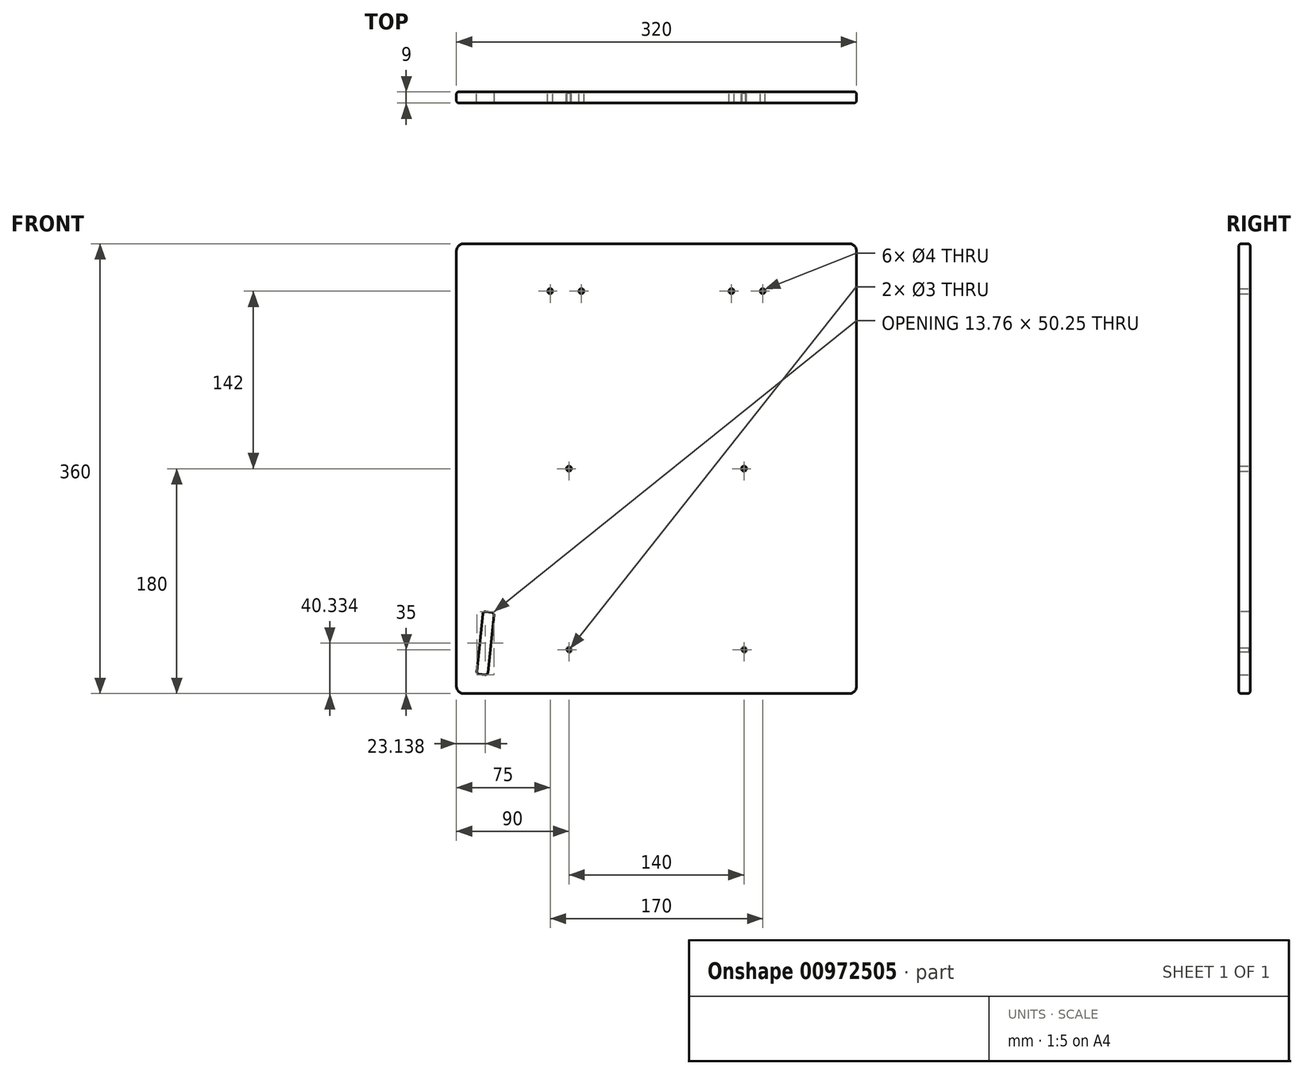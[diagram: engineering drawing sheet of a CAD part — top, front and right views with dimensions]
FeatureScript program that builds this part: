
annotation { "Feature Type Name" : "Feature", "Feature Type Description" : "" }
export const myFeature = defineFeature(function(context is Context, id is Id, definition is map)
    precondition{}
    {
        {
            var Q0;
            Q0=qCreatedBy(makeId("Front.planeOp"),FACE);
            var sketch = newSketch(context, id + "F0", { "sketchPlane" : qUnion([Q0])});
            skLineSegment(sketch, "E0.bottom", {"start": v(-160, 360) * mm, "end": v(160, 360) * mm});
            skLineSegment(sketch, "E0.top", {"start": v(-160, 0) * mm, "end": v(160, 0) * mm});
            skLineSegment(sketch, "E0.left", {"start": v(-160, 360) * mm, "end": v(-160, 0) * mm});
            skLineSegment(sketch, "E0.right", {"start": v(160, 360) * mm, "end": v(160, 0) * mm});
            skSolve(sketch);
        }
        {
            var Q0;
            Q0=makeQuery(id+"F0.imprint","IMPRINT",FACE,{"disambiguationData":[TD([[makeQuery(id+"F0.imprint","IMPRINT",EDGE,{"derivedFrom":sQuery(id+"F0.wireOp",EDGE,"E0.bottom")}),-1.0]])]});
            extrude(context, id + "F1", {"entities" : qUnion([Q0]), "oppositeDirection" : true, "depth" : 9 * mm, "offsetDistance" : 25 * mm});
        }
        {
            var Q0;
            Q0=qCreatedBy(makeId("Front.planeOp"),FACE);
            var sketch = newSketch(context, id + "F2", { "sketchPlane" : qUnion([Q0])});
            skLineSegment(sketch, "E1", {"start": v(-138.72, 65.67) * mm, "end": v(-143.95, 15.94) * mm});
            skLineSegment(sketch, "E2", {"start": v(-135, 15) * mm, "end": v(-129.77, 64.73) * mm});
            skLineSegment(sketch, "E3", {"start": v(-138.72, 65.67) * mm, "end": v(-129.77, 64.73) * mm});
            skLineSegment(sketch, "E4", {"start": v(-143.95, 15.94) * mm, "end": v(-135, 15) * mm});
            skSolve(sketch);
        }
        {
            var Q0;
            Q0=makeQuery(id+"F2.imprint","IMPRINT",FACE,{"disambiguationData":[TD([[makeQuery(id+"F2.imprint","IMPRINT",EDGE,{"derivedFrom":sQuery(id+"F2.wireOp",EDGE,"E1")}),1.0]])]});
            var Q1;
            Q1=makeQuery(id+"F2.imprint","IMPRINT",FACE,{"disambiguationData":[TD([[makeQuery(id+"F2.imprint","IMPRINT",EDGE,{"derivedFrom":sQuery(id+"F2.wireOp",EDGE,"cv69mtFc-LBA8-5CoM-4E6C-DW0wjyTnq0Fr")}),1.0]])]});
            var Q2;
            Q2=makeQuery(id+"F2.imprint","IMPRINT",FACE,{"disambiguationData":[TD([[makeQuery(id+"F2.imprint","IMPRINT",EDGE,{"derivedFrom":sQuery(id+"F2.wireOp",EDGE,"YBglI7SL-vM7m-gSXs-ycqa-cWJAcuNKxBdc.bottom")}),-1.0]])]});
            extrude(context, id + "F3", {"entities" : qUnion([Q0, Q1, Q2]), "operationType" : NewBodyOperationType.REMOVE, "endBound" : BoundingType.THROUGH_ALL, "oppositeDirection" : true, "depth" : 25 * mm, "offsetDistance" : 25 * mm});
        }
        {
            var Q0;
            Q0=makeQuery(id+"F3.boolean.opBoolean","COPY",EDGE,{"derivedFrom":makeQuery(id+"F3.opExtrude","SWEPT_EDGE",EDGE,{"disambiguationData":[OSD([sQuery(id+"F2.wireOp",EDGE,"E2"),sQuery(id+"F2.wireOp",EDGE,"E4")])]})});
            var Q1;
            Q1=makeQuery(id+"F3.boolean.opBoolean","COPY",EDGE,{"derivedFrom":makeQuery(id+"F3.opExtrude","SWEPT_EDGE",EDGE,{"disambiguationData":[OSD([sQuery(id+"F2.wireOp",EDGE,"E1"),sQuery(id+"F2.wireOp",EDGE,"E4")])]})});
            var Q2;
            Q2=makeQuery(id+"F3.boolean.opBoolean","COPY",EDGE,{"derivedFrom":makeQuery(id+"F3.opExtrude","SWEPT_EDGE",EDGE,{"disambiguationData":[OSD([sQuery(id+"F2.wireOp",EDGE,"E2"),sQuery(id+"F2.wireOp",EDGE,"E3")])]})});
            var Q3;
            Q3=makeQuery(id+"F3.boolean.opBoolean","COPY",EDGE,{"derivedFrom":makeQuery(id+"F3.opExtrude","SWEPT_EDGE",EDGE,{"disambiguationData":[OSD([sQuery(id+"F2.wireOp",EDGE,"E1"),sQuery(id+"F2.wireOp",EDGE,"E3")])]})});
            var Q4;
            Q4=makeQuery(id+"F3.boolean.opBoolean","COPY",EDGE,{"derivedFrom":makeQuery(id+"F3.opExtrude","SWEPT_EDGE",EDGE,{"disambiguationData":[OSD([sQuery(id+"F2.wireOp",EDGE,"cv69mtFc-LBA8-5CoM-4E6C-DW0wjyTnq0Fr"),sQuery(id+"F2.wireOp",EDGE,"zAuP8GzA-tnE1-vwlP-NUoL-qnI0OchEDumV")])]})});
            var Q5;
            Q5=makeQuery(id+"F3.boolean.opBoolean","COPY",EDGE,{"derivedFrom":makeQuery(id+"F3.opExtrude","SWEPT_EDGE",EDGE,{"disambiguationData":[OSD([sQuery(id+"F2.wireOp",EDGE,"cv69mtFc-LBA8-5CoM-4E6C-DW0wjyTnq0Fr"),sQuery(id+"F2.wireOp",EDGE,"tRgE08ra-H2Sr-GnxG-apVD-usmjHhvz710O")])]})});
            var Q6;
            Q6=makeQuery(id+"F3.boolean.opBoolean","COPY",EDGE,{"derivedFrom":makeQuery(id+"F3.opExtrude","SWEPT_EDGE",EDGE,{"disambiguationData":[OSD([sQuery(id+"F2.wireOp",EDGE,"zAuP8GzA-tnE1-vwlP-NUoL-qnI0OchEDumV"),sQuery(id+"F2.wireOp",EDGE,"MxeWzJpH-qL4w-clRe-FggT-xUZ2qBjI2IpG")])]})});
            var Q7;
            Q7=makeQuery(id+"F3.boolean.opBoolean","COPY",EDGE,{"derivedFrom":makeQuery(id+"F3.opExtrude","SWEPT_EDGE",EDGE,{"disambiguationData":[OSD([sQuery(id+"F2.wireOp",EDGE,"tRgE08ra-H2Sr-GnxG-apVD-usmjHhvz710O"),sQuery(id+"F2.wireOp",EDGE,"MxeWzJpH-qL4w-clRe-FggT-xUZ2qBjI2IpG")])]})});
            var Q8;
            Q8=makeQuery(id+"F3.boolean.opBoolean","COPY",EDGE,{"derivedFrom":makeQuery(id+"F3.opExtrude","SWEPT_EDGE",EDGE,{"disambiguationData":[OSD([sQuery(id+"F2.wireOp",EDGE,"YBglI7SL-vM7m-gSXs-ycqa-cWJAcuNKxBdc.top"),sQuery(id+"F2.wireOp",EDGE,"YBglI7SL-vM7m-gSXs-ycqa-cWJAcuNKxBdc.right")])]})});
            var Q9;
            Q9=makeQuery(id+"F3.boolean.opBoolean","COPY",EDGE,{"derivedFrom":makeQuery(id+"F3.opExtrude","SWEPT_EDGE",EDGE,{"disambiguationData":[OSD([sQuery(id+"F2.wireOp",EDGE,"YBglI7SL-vM7m-gSXs-ycqa-cWJAcuNKxBdc.top"),sQuery(id+"F2.wireOp",EDGE,"YBglI7SL-vM7m-gSXs-ycqa-cWJAcuNKxBdc.left")])]})});
            var Q10;
            Q10=makeQuery(id+"F3.boolean.opBoolean","COPY",EDGE,{"derivedFrom":makeQuery(id+"F3.opExtrude","SWEPT_EDGE",EDGE,{"disambiguationData":[OSD([sQuery(id+"F2.wireOp",EDGE,"YBglI7SL-vM7m-gSXs-ycqa-cWJAcuNKxBdc.bottom"),sQuery(id+"F2.wireOp",EDGE,"YBglI7SL-vM7m-gSXs-ycqa-cWJAcuNKxBdc.right")])]})});
            var Q11;
            Q11=makeQuery(id+"F3.boolean.opBoolean","COPY",EDGE,{"derivedFrom":makeQuery(id+"F3.opExtrude","SWEPT_EDGE",EDGE,{"disambiguationData":[OSD([sQuery(id+"F2.wireOp",EDGE,"YBglI7SL-vM7m-gSXs-ycqa-cWJAcuNKxBdc.bottom"),sQuery(id+"F2.wireOp",EDGE,"YBglI7SL-vM7m-gSXs-ycqa-cWJAcuNKxBdc.left")])]})});
            fillet(context, id + "F4", {"entities" : qUnion([Q0, Q1, Q2, Q3, Q4, Q5, Q6, Q7, Q8, Q9, Q10, Q11]), "radius" : 2 * mm, "tangentPropagation" : true, "allowEdgeOverflow" : false});
        }
        {
            var Q0;
            Q0=makeQuery(id+"F1.opExtrude","SWEPT_EDGE",EDGE,{"disambiguationData":[OSD([sQuery(id+"F0.wireOp",EDGE,"E0.top"),sQuery(id+"F0.wireOp",EDGE,"E0.right")])]});
            var Q1;
            Q1=makeQuery(id+"F1.opExtrude","SWEPT_EDGE",EDGE,{"disambiguationData":[OSD([sQuery(id+"F0.wireOp",EDGE,"E0.bottom"),sQuery(id+"F0.wireOp",EDGE,"E0.right")])]});
            var Q2;
            Q2=makeQuery(id+"F1.opExtrude","SWEPT_EDGE",EDGE,{"disambiguationData":[OSD([sQuery(id+"F0.wireOp",EDGE,"E0.bottom"),sQuery(id+"F0.wireOp",EDGE,"E0.left")])]});
            var Q3;
            Q3=makeQuery(id+"F1.opExtrude","SWEPT_EDGE",EDGE,{"disambiguationData":[OSD([sQuery(id+"F0.wireOp",EDGE,"E0.top"),sQuery(id+"F0.wireOp",EDGE,"E0.left")])]});
            fillet(context, id + "F5", {"entities" : qUnion([Q0, Q1, Q2, Q3]), "radius" : 6 * mm, "tangentPropagation" : true, "allowEdgeOverflow" : false});
        }
        {
            var Q0;
            Q0=makeQuery(id+"F1.opExtrude","CAP_FACE",FACE,{"disambiguationData":[OSD([sQuery(id+"F0.wireOp",EDGE,"E0.bottom"),sQuery(id+"F0.wireOp",EDGE,"E0.top"),sQuery(id+"F0.wireOp",EDGE,"E0.left"),sQuery(id+"F0.wireOp",EDGE,"E0.right")])],"isStart":false});
            var sketch = newSketch(context, id + "F6", { "sketchPlane" : qUnion([Q0])});
            skPoint(sketch, "E5", {"position": v(-70, 35) * mm});
            skPoint(sketch, "E6", {"position": v(70, 35) * mm});
            skLineSegment(sketch, "E7", {"start": v(-70, 35) * mm, "end": v(70, 35) * mm, "construction": true});
            skLineSegment(sketch, "E8", {"start": v(0, 35) * mm, "end": v(0, 0) * mm, "construction": true});
            skSolve(sketch);
        }
        {
            var Q0;
            Q0=sQuery(id+"F6.wireOp",VERTEX,"E5");
            var Q1;
            Q1=sQuery(id+"F6.wireOp",VERTEX,"E6");
            var Q2;
            Q2=makeQuery(id+"F1.opExtrude","SWEPT_BODY",BODY,{"disambiguationData":[OSD([sQuery(id+"F0.wireOp",EDGE,"E0.bottom"),sQuery(id+"F0.wireOp",EDGE,"E0.top"),sQuery(id+"F0.wireOp",EDGE,"E0.left"),sQuery(id+"F0.wireOp",EDGE,"E0.right")])]});
            hole(context, id + "F7", {"style" : HoleStyle.C_SINK, "endStyle" : HoleEndStyle.THROUGH, "holeDiameter" : 3 * mm, "cSinkDiameter" : 5 * mm, "cSinkAngle" : 90 * degree, "majorDiameter" : 5 * mm, "isTappedThrough" : true, "tappedDepth" : 12 * mm, "tapClearance" : 3, "locations" : qUnion([Q0, Q1]), "scope" : qUnion([Q2])});
        }
        {
            var Q0;
            Q0=makeQuery(id+"F1.opExtrude","CAP_FACE",FACE,{"disambiguationData":[OSD([sQuery(id+"F0.wireOp",EDGE,"E0.bottom"),sQuery(id+"F0.wireOp",EDGE,"E0.top"),sQuery(id+"F0.wireOp",EDGE,"E0.left"),sQuery(id+"F0.wireOp",EDGE,"E0.right")])],"isStart":false});
            var sketch = newSketch(context, id + "F8", { "sketchPlane" : qUnion([Q0])});
            skLineSegment(sketch, "E9", {"start": v(-70, 180) * mm, "end": v(70, 180) * mm, "construction": true});
            skLineSegment(sketch, "E10", {"start": v(0, 180) * mm, "end": v(0, 0) * mm, "construction": true});
            skPoint(sketch, "E11", {"position": v(-70, 180) * mm});
            skPoint(sketch, "E12", {"position": v(70, 180) * mm});
            skLineSegment(sketch, "E13", {"start": v(85, 322) * mm, "end": v(60, 322) * mm, "construction": true});
            skPoint(sketch, "E14", {"position": v(85, 322) * mm});
            skPoint(sketch, "E15", {"position": v(60, 322) * mm});
            skPoint(sketch, "E16", {"position": v(-60, 322) * mm});
            skPoint(sketch, "E17", {"position": v(-85, 322) * mm});
            skLineSegment(sketch, "E18", {"start": v(60, 322) * mm, "end": v(-60, 322) * mm, "construction": true});
            skLineSegment(sketch, "E19", {"start": v(-60, 322) * mm, "end": v(-85, 322) * mm, "construction": true});
            skLineSegment(sketch, "E20", {"start": v(0, 180) * mm, "end": v(0, 322) * mm, "construction": true});
            skSolve(sketch);
        }
        {
            var Q0;
            Q0=sQuery(id+"F8.wireOp",VERTEX,"E9.start");
            var Q1;
            Q1=sQuery(id+"F8.wireOp",VERTEX,"E12");
            var Q2;
            Q2=sQuery(id+"F8.wireOp",VERTEX,"E14");
            var Q3;
            Q3=sQuery(id+"F8.wireOp",VERTEX,"E13.end");
            var Q4;
            Q4=sQuery(id+"F8.wireOp",VERTEX,"E16");
            var Q5;
            Q5=sQuery(id+"F8.wireOp",VERTEX,"E17");
            var Q6;
            Q6=makeQuery(id+"F1.opExtrude","SWEPT_BODY",BODY,{"disambiguationData":[OSD([sQuery(id+"F0.wireOp",EDGE,"E0.bottom"),sQuery(id+"F0.wireOp",EDGE,"E0.top"),sQuery(id+"F0.wireOp",EDGE,"E0.left"),sQuery(id+"F0.wireOp",EDGE,"E0.right")])]});
            hole(context, id + "F9", {"style" : HoleStyle.SIMPLE, "endStyle" : HoleEndStyle.THROUGH, "holeDiameter" : 4 * mm, "majorDiameter" : 5 * mm, "isTappedThrough" : true, "tappedDepth" : 12 * mm, "tapClearance" : 3, "locations" : qUnion([Q0, Q1, Q2, Q3, Q4, Q5]), "scope" : qUnion([Q6])});
        }
        {
            var Q0;
            Q0=makeQuery(id+"F1.opExtrude","CAP_EDGE",EDGE,{"disambiguationData":[OSD([sQuery(id+"F0.wireOp",EDGE,"E0.right")])],"isStart":false});
            var Q1;
            Q1=makeQuery(id+"F1.opExtrude","CAP_EDGE",EDGE,{"disambiguationData":[OSD([sQuery(id+"F0.wireOp",EDGE,"E0.right")])],"isStart":true});
            var Q2;
            Q2=makeQuery(id+"FP4PKnZbiEjVcH8_1.boolean.opBoolean","COPY",EDGE,{"derivedFrom":makeQuery(id+"FP4PKnZbiEjVcH8_1.opExtrude","CAP_EDGE",EDGE,{"disambiguationData":[OSD([sQuery(id+"F2zITgzdlax0r63_1.wireOp",EDGE,"F9WBHKQW-thjq-v7hr-UK5a-oQhZYT8kJ9Dk.left")])],"isStart":true})});
            var Q3;
            Q3=makeQuery(id+"FP4PKnZbiEjVcH8_1.boolean.opBoolean","INTERSECT",EDGE,{"derivedFrom":[makeQuery(id+"F1.opExtrude","CAP_FACE",FACE,{"disambiguationData":[OSD([sQuery(id+"F0.wireOp",EDGE,"E0.bottom"),sQuery(id+"F0.wireOp",EDGE,"E0.top"),sQuery(id+"F0.wireOp",EDGE,"E0.left"),sQuery(id+"F0.wireOp",EDGE,"E0.right")])],"isStart":false}),makeQuery(id+"FP4PKnZbiEjVcH8_1.opExtrude","SWEPT_FACE",FACE,{"disambiguationData":[OSD([sQuery(id+"F2zITgzdlax0r63_1.wireOp",EDGE,"F9WBHKQW-thjq-v7hr-UK5a-oQhZYT8kJ9Dk.left")])]})]});
            fillet(context, id + "F10", {"entities" : qUnion([Q0, Q1, Q2, Q3]), "radius" : 2 * mm, "tangentPropagation" : true, "allowEdgeOverflow" : false});
        }
    });
